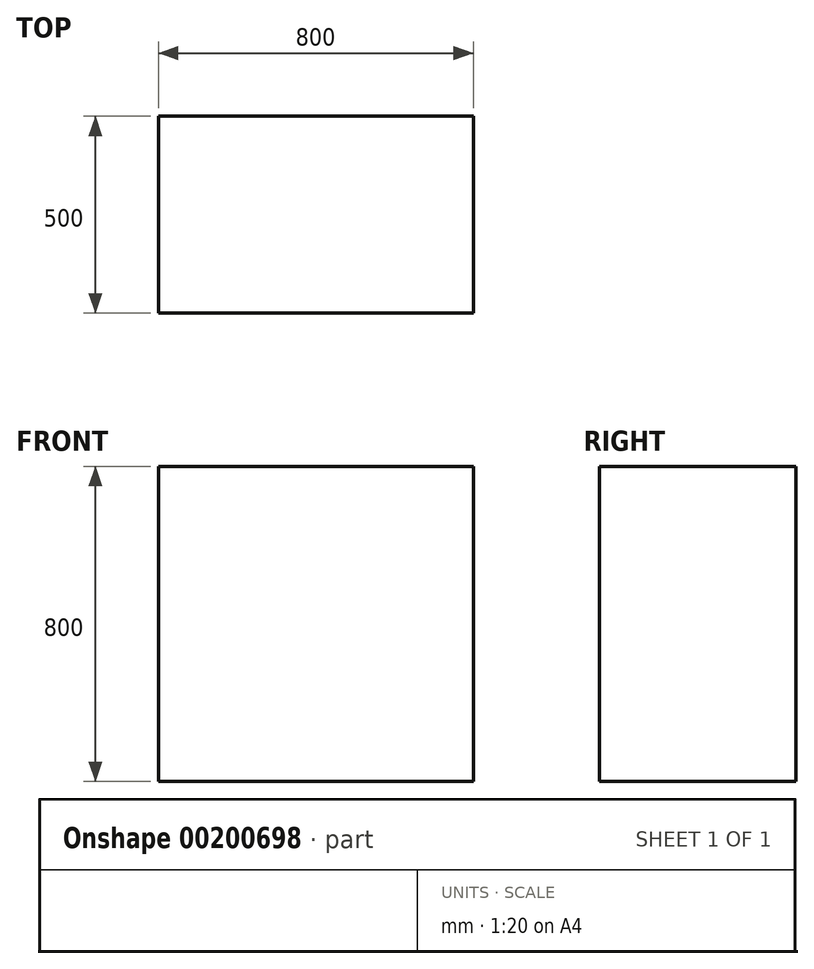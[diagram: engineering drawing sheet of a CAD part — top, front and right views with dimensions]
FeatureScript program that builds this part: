
annotation { "Feature Type Name" : "Feature", "Feature Type Description" : "" }
export const myFeature = defineFeature(function(context is Context, id is Id, definition is map)
    precondition{}
    {
        {
            var Q0;
            Q0=qCreatedBy(makeId("Front.planeOp"),FACE);
            var sketch = newSketch(context, id + "F0", { "sketchPlane" : qUnion([Q0])});
            skLineSegment(sketch, "E0.bottom", {"start": v(0, 0) * mm, "end": v(800, 0) * mm});
            skLineSegment(sketch, "E0.top", {"start": v(0, 800) * mm, "end": v(800, 800) * mm});
            skLineSegment(sketch, "E0.left", {"start": v(0, 0) * mm, "end": v(0, 800) * mm});
            skLineSegment(sketch, "E0.right", {"start": v(800, 0) * mm, "end": v(800, 800) * mm});
            skSolve(sketch);
        }
        {
            var Q0;
            Q0 = qSketchRegion(id + "F0", true);
            extrude(context, id + "F1", {"entities" : qUnion([Q0]), "depth" : 500 * mm});
        }
    });
